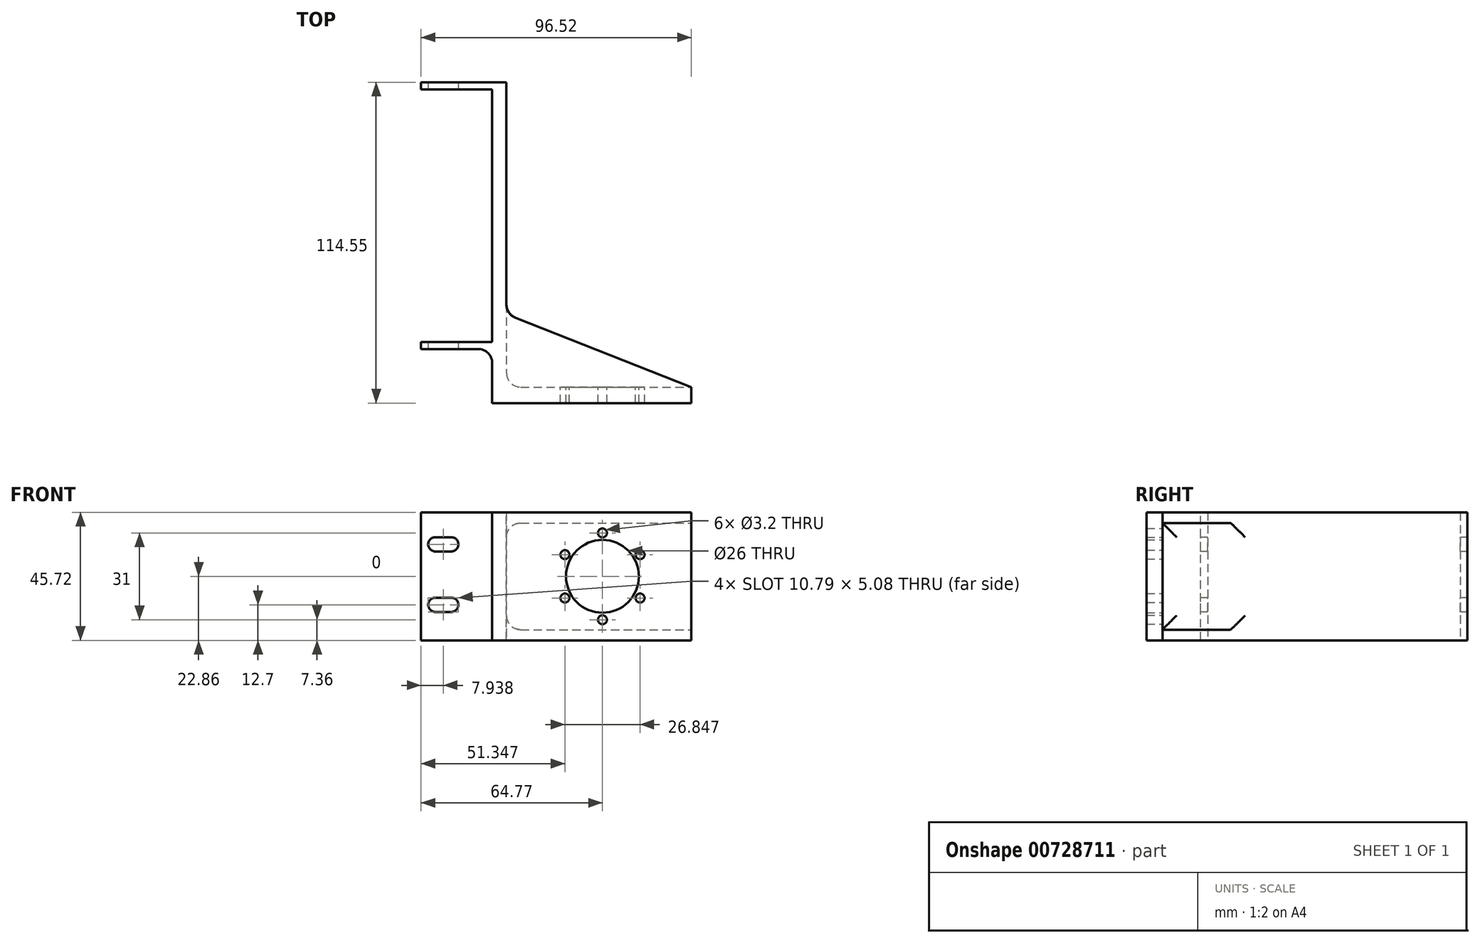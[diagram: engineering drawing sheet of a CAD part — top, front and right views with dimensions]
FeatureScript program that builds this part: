
annotation { "Feature Type Name" : "Feature", "Feature Type Description" : "" }
export const myFeature = defineFeature(function(context is Context, id is Id, definition is map)
    precondition{}
    {
        {
            var Q0;
            Q0=qCreatedBy(makeId("Right.planeOp"),FACE);
            var sketch = newSketch(context, id + "F0", { "sketchPlane" : qUnion([Q0])});
            skLineSegment(sketch, "E0", {"start": v(0, 0) * mm, "end": v(0, -45.72) * mm});
            skLineSegment(sketch, "E1", {"start": v(0, -45.72) * mm, "end": v(95.25, -45.72) * mm});
            skLineSegment(sketch, "E2", {"start": v(95.25, -45.72) * mm, "end": v(95.25, 0) * mm});
            skLineSegment(sketch, "E3", {"start": v(95.25, 0) * mm, "end": v(0, 0) * mm});
            skSolve(sketch);
        }
        {
            var Q0;
            Q0 = qSketchRegion(id + "F0", true);
            extrude(context, id + "F1", {"entities" : qUnion([Q0]), "depth" : 5.08 * mm, "offsetDistance" : 25.4 * mm});
        }
        {
            var Q0;
            Q0=qCreatedBy(makeId("Right.planeOp"),FACE);
            var sketch = newSketch(context, id + "F2", { "sketchPlane" : qUnion([Q0])});
            skLineSegment(sketch, "E4.bottom", {"start": v(95.25, 0) * mm, "end": v(92.7, 0) * mm});
            skLineSegment(sketch, "E4.top", {"start": v(95.25, -45.72) * mm, "end": v(92.71, -45.72) * mm});
            skLineSegment(sketch, "E4.left", {"start": v(95.25, 0) * mm, "end": v(95.25, -45.72) * mm});
            skLineSegment(sketch, "E4.right", {"start": v(92.7, 0) * mm, "end": v(92.71, -45.72) * mm});
            skLineSegment(sketch, "E5.bottom", {"start": v(0, 0) * mm, "end": v(2.54, 0) * mm});
            skLineSegment(sketch, "E5.top", {"start": v(0, -45.72) * mm, "end": v(2.54, -45.72) * mm});
            skLineSegment(sketch, "E5.left", {"start": v(0, 0) * mm, "end": v(0, -45.72) * mm});
            skLineSegment(sketch, "E5.right", {"start": v(2.54, 0) * mm, "end": v(2.54, -45.72) * mm});
            skSolve(sketch);
        }
        {
            var Q0;
            Q0 = qSketchRegion(id + "F2", true);
            extrude(context, id + "F3", {"entities" : qUnion([Q0]), "operationType" : NewBodyOperationType.ADD, "oppositeDirection" : true, "depth" : 25.4 * mm, "offsetDistance" : 25.4 * mm});
        }
        {
            var Q0;
            Q0=qCreatedBy(makeId("Front.planeOp"),FACE);
            var sketch = newSketch(context, id + "F4", { "sketchPlane" : qUnion([Q0])});
            skArc(sketch, "E6", {"start": v(-14.6, -13.97) * mm, "mid": v(-12.06, -11.43) * mm, "end": v(-14.6, -8.89) * mm});
            skArc(sketch, "E7", {"start": v(-14.6, -35.56) * mm, "mid": v(-12.06, -33.02) * mm, "end": v(-14.6, -30.48) * mm});
            skLineSegment(sketch, "E8", {"start": v(-14.6, -11.43) * mm, "end": v(-14.6, -33.02) * mm, "construction": true});
            skArc(sketch, "E9", {"start": v(-20.32, -30.48) * mm, "mid": v(-22.86, -33.02) * mm, "end": v(-20.32, -35.56) * mm});
            skArc(sketch, "E10", {"start": v(-20.32, -8.89) * mm, "mid": v(-22.86, -11.43) * mm, "end": v(-20.32, -13.97) * mm});
            skLineSegment(sketch, "E11", {"start": v(-14.6, -35.56) * mm, "end": v(-20.32, -35.56) * mm});
            skLineSegment(sketch, "E12", {"start": v(-14.6, -30.48) * mm, "end": v(-20.32, -30.48) * mm});
            skLineSegment(sketch, "E13", {"start": v(-14.6, -13.97) * mm, "end": v(-20.32, -13.97) * mm});
            skLineSegment(sketch, "E14", {"start": v(-14.6, -8.89) * mm, "end": v(-20.32, -8.89) * mm});
            skSolve(sketch);
        }
        {
            var Q0;
            Q0 = qSketchRegion(id + "F4", true);
            extrude(context, id + "F5", {"entities" : qUnion([Q0]), "operationType" : NewBodyOperationType.REMOVE, "endBound" : BoundingType.THROUGH_ALL, "oppositeDirection" : true, "depth" : 25.4 * mm, "offsetDistance" : 25.4 * mm, "hasSecondDirection" : true, "secondDirectionBound" : BoundingType.THROUGH_ALL, "secondDirectionOppositeDirection" : false, "secondDirectionDepth" : 25.4 * mm});
        }
        {
            var Q0;
            Q0=makeQuery(id+"F1.opExtrude","CAP_EDGE",EDGE,{"disambiguationData":[OSD([sQuery(id+"F0.wireOp",EDGE,"E0")])],"isStart":false});
            cPoint(context, id + "F6", {"entities" : qUnion([Q0]), "parameter" : 0.5});
        }
        {
            var Q0;
            Q0=qCreatedBy(makeId("Top.planeOp"),FACE);
            var Q1;
            Q1 = qCreatedBy(id + "F6" ,VERTEX);
            cPlane(context, id + "F7", {"entities" : qUnion([Q0, Q1]), "cplaneType" : CPlaneType.PLANE_POINT, "offset" : 25.4 * mm, "width" : 152.4 * mm, "height" : 152.4 * mm});
        }
        {
            var Q0;
            Q0=qCreatedBy(id+"F7.planeOp",FACE);
            var sketch = newSketch(context, id + "F8", { "sketchPlane" : qUnion([Q0])});
            skLineSegment(sketch, "E15", {"start": v(71.12, -13.59) * mm, "end": v(0, -13.59) * mm, "construction": true});
            skLineSegment(sketch, "E16.bottom", {"start": v(0, 12.45) * mm, "end": v(71.12, 12.45) * mm});
            skLineSegment(sketch, "E16.top", {"start": v(0, -19.3) * mm, "end": v(71.12, -19.3) * mm});
            skLineSegment(sketch, "E16.left", {"start": v(0, 12.45) * mm, "end": v(0, -19.3) * mm});
            skLineSegment(sketch, "E16.right", {"start": v(71.12, 12.45) * mm, "end": v(71.12, -19.3) * mm});
            skLineSegment(sketch, "E17", {"start": v(39.37, -13.59) * mm, "end": v(39.37, 95.25) * mm, "construction": true});
            skLineSegment(sketch, "E18", {"start": v(-36.83, -13.59) * mm, "end": v(-36.83, 95.25) * mm, "construction": true});
            skSolve(sketch);
        }
        {
            var Q0;
            Q0 = qSketchRegion(id + "F8", true);
            var Q1;
            Q1=makeQuery(id+"F3.boolean.opBoolean","MERGE",FACE,{"derivedFrom":[makeQuery(id+"F1.opExtrude","SWEPT_FACE",FACE,{"disambiguationData":[OSD([sQuery(id+"F0.wireOp",EDGE,"E1")])]}),makeQuery(id+"F3.opExtrude","SWEPT_FACE",FACE,{"disambiguationData":[OSD([sQuery(id+"F2.wireOp",EDGE,"E4.top")])]}),makeQuery(id+"F3.opExtrude","SWEPT_FACE",FACE,{"disambiguationData":[OSD([sQuery(id+"F2.wireOp",EDGE,"E5.top")])]})]});
            var Q2;
            Q2=makeQuery(id+"F3.boolean.opBoolean","MERGE",FACE,{"derivedFrom":[makeQuery(id+"F1.opExtrude","SWEPT_FACE",FACE,{"disambiguationData":[OSD([sQuery(id+"F0.wireOp",EDGE,"E3")])]}),makeQuery(id+"F3.opExtrude","SWEPT_FACE",FACE,{"disambiguationData":[OSD([sQuery(id+"F2.wireOp",EDGE,"E4.bottom")])]}),makeQuery(id+"F3.opExtrude","SWEPT_FACE",FACE,{"disambiguationData":[OSD([sQuery(id+"F2.wireOp",EDGE,"E5.bottom")])]})]});
            extrude(context, id + "F9", {"entities" : qUnion([Q0]), "operationType" : NewBodyOperationType.ADD, "endBound" : BoundingType.UP_TO_SURFACE, "oppositeDirection" : true, "depth" : 25.4 * mm, "endBoundEntityFace" : qUnion([Q1]), "offsetDistance" : 25.4 * mm, "hasSecondDirection" : true, "secondDirectionBound" : BoundingType.UP_TO_SURFACE, "secondDirectionOppositeDirection" : false, "secondDirectionDepth" : 25.4 * mm, "secondDirectionBoundEntityFace" : qUnion([Q2])});
        }
        {
            var Q0;
            Q0=qCreatedBy(makeId("Front.planeOp"),FACE);
            var sketch = newSketch(context, id + "F10", { "sketchPlane" : qUnion([Q0])});
            skLineSegment(sketch, "E19.bottom", {"start": v(5.08, -3.81) * mm, "end": v(71.12, -3.8) * mm});
            skLineSegment(sketch, "E19.top", {"start": v(5.08, -41.91) * mm, "end": v(71.12, -41.91) * mm});
            skLineSegment(sketch, "E19.left", {"start": v(5.08, -3.81) * mm, "end": v(5.08, -41.91) * mm});
            skLineSegment(sketch, "E19.right", {"start": v(71.12, -3.81) * mm, "end": v(71.12, -41.91) * mm});
            skSolve(sketch);
        }
        {
            var Q0;
            Q0 = qSketchRegion(id + "F10", true);
            var Q1;
            Q1=sQuery(id+"F8.wireOp",VERTEX,"E17.start");
            extrude(context, id + "F11", {"entities" : qUnion([Q0]), "operationType" : NewBodyOperationType.REMOVE, "endBound" : BoundingType.THROUGH_ALL, "oppositeDirection" : true, "depth" : 25.4 * mm, "offsetDistance" : 25.4 * mm, "hasSecondDirection" : true, "secondDirectionBound" : BoundingType.UP_TO_VERTEX, "secondDirectionOppositeDirection" : false, "secondDirectionDepth" : 25.4 * mm, "secondDirectionBoundEntityVertex" : qUnion([Q1])});
        }
        {
            var Q0;
            Q0=qCreatedBy(makeId("Top.planeOp"),FACE);
            var sketch = newSketch(context, id + "F12", { "sketchPlane" : qUnion([Q0])});
            skLineSegment(sketch, "E20", {"start": v(71.12, -13.59) * mm, "end": v(5.08, 12.45) * mm});
            skLineSegment(sketch, "E21", {"start": v(71.12, -13.59) * mm, "end": v(71.12, 12.45) * mm});
            skLineSegment(sketch, "E22", {"start": v(71.12, 12.45) * mm, "end": v(5.08, 12.45) * mm});
            skSolve(sketch);
        }
        {
            var Q0;
            Q0 = qSketchRegion(id + "F12", true);
            extrude(context, id + "F13", {"entities" : qUnion([Q0]), "operationType" : NewBodyOperationType.REMOVE, "endBound" : BoundingType.THROUGH_ALL, "oppositeDirection" : true, "depth" : 25.4 * mm, "offsetDistance" : 25.4 * mm, "hasSecondDirection" : true, "secondDirectionBound" : BoundingType.THROUGH_ALL, "secondDirectionOppositeDirection" : false, "secondDirectionDepth" : 25.4 * mm});
        }
        {
            var Q0;
            Q0=qCreatedBy(makeId("Front.planeOp"),FACE);
            var sketch = newSketch(context, id + "F14", { "sketchPlane" : qUnion([Q0])});
            skCircle(sketch, "E23", {"center": v(39.37, -22.86) * mm, "radius": 18.5 * mm, "construction": true});
            skCircle(sketch, "E24", {"center": v(39.37, -7.36) * mm, "radius": 1.6 * mm});
            skLineSegment(sketch, "E25", {"start": v(39.37, -7.36) * mm, "end": v(39.37, -22.86) * mm, "construction": true});
            skCircle(sketch, "E26.1.0", {"center": v(25.95, -15.1) * mm, "radius": 1.6 * mm});
            skCircle(sketch, "E26.2.0", {"center": v(25.95, -30.6) * mm, "radius": 1.6 * mm});
            skCircle(sketch, "E26.3.0", {"center": v(39.37, -38.36) * mm, "radius": 1.6 * mm});
            skCircle(sketch, "E26.4.0", {"center": v(52.8, -30.61) * mm, "radius": 1.6 * mm});
            skCircle(sketch, "E26.5.0", {"center": v(52.8, -15.11) * mm, "radius": 1.6 * mm});
            skCircle(sketch, "E27", {"center": v(39.37, -22.86) * mm, "radius": 13 * mm});
            skSolve(sketch);
        }
        {
            var Q0;
            Q0 = qSketchRegion(id + "F14", true);
            extrude(context, id + "F15", {"entities" : qUnion([Q0]), "operationType" : NewBodyOperationType.REMOVE, "endBound" : BoundingType.THROUGH_ALL, "depth" : 25.4 * mm, "offsetDistance" : 25.4 * mm});
        }
        {
            var Q0;
            Q0=makeQuery(id+"F3.opExtrude","CAP_EDGE",EDGE,{"disambiguationData":[OSD([sQuery(id+"F2.wireOp",EDGE,"E4.right")])],"isStart":true});
            var Q1;
            Q1=makeQuery(id+"F3.opExtrude","CAP_EDGE",EDGE,{"disambiguationData":[OSD([sQuery(id+"F2.wireOp",EDGE,"E5.right")])],"isStart":true});
            var Q2;
            Q2=makeQuery(id+"F9.boolean.opBoolean","INTERSECT",EDGE,{"derivedFrom":[makeQuery(id+"F3.boolean.opBoolean","MERGE",FACE,{"derivedFrom":[makeQuery(id+"F1.opExtrude","SWEPT_FACE",FACE,{"disambiguationData":[OSD([sQuery(id+"F0.wireOp",EDGE,"E0")])]}),makeQuery(id+"F3.opExtrude","SWEPT_FACE",FACE,{"disambiguationData":[OSD([sQuery(id+"F2.wireOp",EDGE,"E5.left")])]})]}),makeQuery(id+"F9.opExtrude","SWEPT_FACE",FACE,{"disambiguationData":[OSD([sQuery(id+"F8.wireOp",EDGE,"E16.left")])]})]});
            var Q3;
            Q3=makeQuery(id+"F9.opExtrude","TWEAK_EDGE",EDGE,{"derivedFrom":[makeQuery(id+"F8.imprint","IMPRINT",EDGE,{"derivedFrom":sQuery(id+"F8.wireOp",EDGE,"E16.top")}),makeQuery(id+"F8.imprint","IMPRINT",EDGE,{"derivedFrom":sQuery(id+"F8.wireOp",EDGE,"E16.left")})]});
            var Q4;
            Q4=makeQuery(id+"F11.boolean.opBoolean","COPY",EDGE,{"derivedFrom":makeQuery(id+"F11.opExtrude","CAP_EDGE",EDGE,{"disambiguationData":[OSD([sQuery(id+"F10.wireOp",EDGE,"E19.left")])],"isStart":true})});
            var Q5;
            Q5=makeQuery(id+"F11.boolean.opBoolean","COPY",EDGE,{"derivedFrom":makeQuery(id+"F11.opExtrude","SWEPT_EDGE",EDGE,{"disambiguationData":[OSD([sQuery(id+"F10.wireOp",EDGE,"E19.bottom"),sQuery(id+"F10.wireOp",EDGE,"E19.left")])]})});
            var Q6;
            Q6=makeQuery(id+"F11.boolean.opBoolean","COPY",EDGE,{"derivedFrom":makeQuery(id+"F11.opExtrude","SWEPT_EDGE",EDGE,{"disambiguationData":[OSD([sQuery(id+"F10.wireOp",EDGE,"E19.top"),sQuery(id+"F10.wireOp",EDGE,"E19.left")])]})});
            var Q7;
            {var subQ0=sQuery(id+"F0.wireOp",EDGE,"E3");var subQ1=makeQuery(id+"F1.opExtrude","CAP_FACE",FACE,{"disambiguationData":[OSD([sQuery(id+"F0.wireOp",EDGE,"E0"),sQuery(id+"F0.wireOp",EDGE,"E1"),sQuery(id+"F0.wireOp",EDGE,"E2"),subQ0])],"isStart":false});var subQ2=sQuery(id+"F8.wireOp",EDGE,"E16.bottom");var subQ3=makeQuery(id+"F9.opExtrude","SWEPT_FACE",FACE,{"disambiguationData":[OSD([subQ2])]});Q7=makeQuery(id+"F13.boolean.opBoolean","MERGE",EDGE,{"derivedFrom":[makeQuery(id+"F11.boolean.opBoolean","SPLIT",EDGE,{"disambiguationData":[TD([makeQuery(id+"F1.opExtrude","SWEPT_FACE",FACE,{"disambiguationData":[OSD([subQ0])]})])],"derivedFrom":makeQuery(id+"F9.boolean.opBoolean","INTERSECT",EDGE,{"derivedFrom":[subQ1,subQ3]})})],"fromTools":[makeQuery(id+"F13.opExtrude","SWEPT_EDGE",EDGE,{"disambiguationData":[OSD([sQuery(id+"F12.wireOp",EDGE,"E20"),sQuery(id+"F12.wireOp",EDGE,"E22")])]})]});}
            var Q8;
            {var subQ0=sQuery(id+"F0.wireOp",EDGE,"E1");var subQ1=sQuery(id+"F8.wireOp",EDGE,"E16.bottom");var subQ2=makeQuery(id+"F1.opExtrude","CAP_FACE",FACE,{"disambiguationData":[OSD([sQuery(id+"F0.wireOp",EDGE,"E0"),subQ0,sQuery(id+"F0.wireOp",EDGE,"E2"),sQuery(id+"F0.wireOp",EDGE,"E3")])],"isStart":false});var subQ3=makeQuery(id+"F9.opExtrude","SWEPT_FACE",FACE,{"disambiguationData":[OSD([subQ1])]});Q8=makeQuery(id+"F13.boolean.opBoolean","MERGE",EDGE,{"derivedFrom":[makeQuery(id+"F11.boolean.opBoolean","SPLIT",EDGE,{"disambiguationData":[TD([makeQuery(id+"F1.opExtrude","SWEPT_FACE",FACE,{"disambiguationData":[OSD([subQ0])]})])],"derivedFrom":makeQuery(id+"F9.boolean.opBoolean","INTERSECT",EDGE,{"derivedFrom":[subQ2,subQ3]})})],"fromTools":[makeQuery(id+"F13.opExtrude","SWEPT_EDGE",EDGE,{"disambiguationData":[OSD([sQuery(id+"F12.wireOp",EDGE,"E20"),sQuery(id+"F12.wireOp",EDGE,"E22")])]})]});}
            var Q9;
            Q9=makeQuery(id+"F1.opExtrude","CAP_EDGE",EDGE,{"disambiguationData":[OSD([sQuery(id+"F0.wireOp",EDGE,"E2")])],"isStart":false});
            fillet(context, id + "F16", {"entities" : qUnion([Q0, Q1, Q2, Q3, Q4, Q5, Q6, Q7, Q8, Q9]), "tangentPropagation" : true, "radius" : 5.08 * mm, "defaultsChanged" : false, "vertexSettings" : [], "allowEdgeOverflow" : false});
        }
    });
